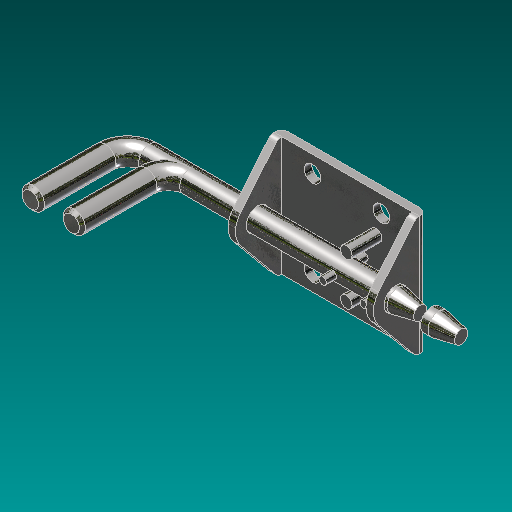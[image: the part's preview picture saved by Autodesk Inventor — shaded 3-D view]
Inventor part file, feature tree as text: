
AUTODESK INVENTOR PART (.ipt)
format: ipt  version: 2017 (Build 210142000, 142)  size: 283,648 bytes
history: native  units: in
note: dims shown in document units (in); Inventor stores cm internally (conversion verified against a paired STEP export)
features: sketch x8, extrude x5, chamfer x3, hole x2, shell x1, fillet x1, sweep x1, plane x1, pattern_linear x1, other x1
ambient origin geometry x8: Origin, YZ Plane, XZ Plane, XY Plane, X Axis, Y Axis, Z Axis, Center Point
bodies: Solid1 (feature_tree)
feature tree (24):
  extrude  "Extrusion1"  Depth=2.0in
  extrude  "Extrusion2"  Depth=0.125in
  shell  "Shell1"  Thickness=0.125in
  fillet  "Fillet1"  Radius=0.9in
  hole  "Hole1"  [1 undecoded]
  hole  "Hole2"  [1 undecoded]
  sweep  "Sweep1"
  chamfer  "Chamfer1"  Distance=1.1in
  chamfer  "Chamfer2"  Distance=1.375in
  extrude  "Extrusion3"  Depth=0.6875in
  plane  "Work Plane1"
  extrude  "Extrusion4"  Depth=0.6875in
  pattern_linear  "Rectangular Pattern1"  Spacing1=0.371in  [1 undecoded]
  extrude  "Extrusion5"  TaperAngle=0.0deg  [1 undecoded]
  chamfer  "Chamfer3"  Distance=0.05in Angle=45.0deg
  sketch  "Sketch1"  dims[d0=2.4375in d1=2.0in]
  sketch  "Sketch2"  dims[d2=1.0in d3=0.0in d4=0.125in d5=0.125in d6=0.9in]
  sketch  "Sketch3"  dims[d7=0.375in d8=1.0in d9=0.0in]
  sketch  "Sketch4"  dims[d10=0.125in d11=0.125in]
  sketch  "Sketch5"  dims[d12=1.0in d13=1.0in]
  sketch  "Sketch6"  dims[d14=0.3906in d15=0.75in d16=0.375in d17=0.25in d18=0.5635in d19=1.0in d20=0.8108in d21=1.1562in]
  other  "Work Axis1"
  sketch  "Sketch7"  dims[d22=1.4375in]
  sketch  "Sketch8"  dims[d23=0.277in d24=0.75in d25=0.375in d26=0.25in d27=0.5635in d28=1.0in d29=0.8108in d30=1.1in d31=1.375in d32=0.375in d33=1.625in d34=0.371in d35=0.0in d36=0.05in d37=0.125in d38=45.0deg d39=0.375in d40=0.125in d41=0.0756in d42=0.1969in d44=0.506in d45=0.7188in d46=0.5in d47=0.0in d48=0.0in d49=0.125in d50=0.7in d51=0.0in d52=0.7874in d54=0.6875in d55=0.5in d56=0.6875in d57=0.7in d58=0.0in d59=0.375in d60=0.125in d61=0.0756in d62=0.0in]
note: 4 required parameter values undecoded (feature->parameter linkage not recoverable at this tier; creation-order binding heuristic only, values carry confidence <= 0.55)
